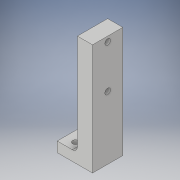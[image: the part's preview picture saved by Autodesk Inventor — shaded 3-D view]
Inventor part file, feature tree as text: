
AUTODESK INVENTOR PART (.ipt)
format: ipt  version: 2017 (Build 210142000, 142)  size: 135,680 bytes
history: native  units: in
note: dims shown in document units (in); Inventor stores cm internally (conversion verified against a paired STEP export)
features: sketch x4, projected_geometry x3, extrude x2, hole x2, fillet x1
ambient origin geometry x8: Origin, YZ Plane, XZ Plane, XY Plane, X Axis, Y Axis, Z Axis, Center Point
bodies: Solid1 (feature_tree)
feature tree (12):
  extrude  "Extrusion1"  Depth=2.75in
  hole  "Hole1"  [1 undecoded]
  extrude  "Extrusion2"  Depth=2.75in
  hole  "Hole3"  [1 undecoded]
  fillet  "Fillet1"  Radius=0.375in
  sketch  "Sketch1"  dims[d0=0.75in d1=2.75in]
  sketch  "Sketch2"  dims[d2=0.375in d3=0.0in d4=1.061in]
  projected_geometry  "Projected Loop1"
  sketch  "Sketch5"  dims[d5=0.75in d6=2.75in]
  projected_geometry  "Projected Loop3"
  sketch  "Sketch6"  dims[d7=0.125in d8=0.375in d9=0.375in d10=0.14in d11=0.75in d12=0.375in d13=0.25in d14=0.5635in d15=1.0in d16=0.8108in d31=0.25in d32=0.5in d33=0.0in d34=0.75in d35=0.2in d36=0.2in d37=0.14in d38=0.75in d39=0.375in d40=0.25in d41=0.5635in d42=1.0in d43=0.8108in d44=0.125in]
  projected_geometry  "Projected Loop4"
note: 2 required parameter values undecoded (feature->parameter linkage not recoverable at this tier; creation-order binding heuristic only, values carry confidence <= 0.55)
